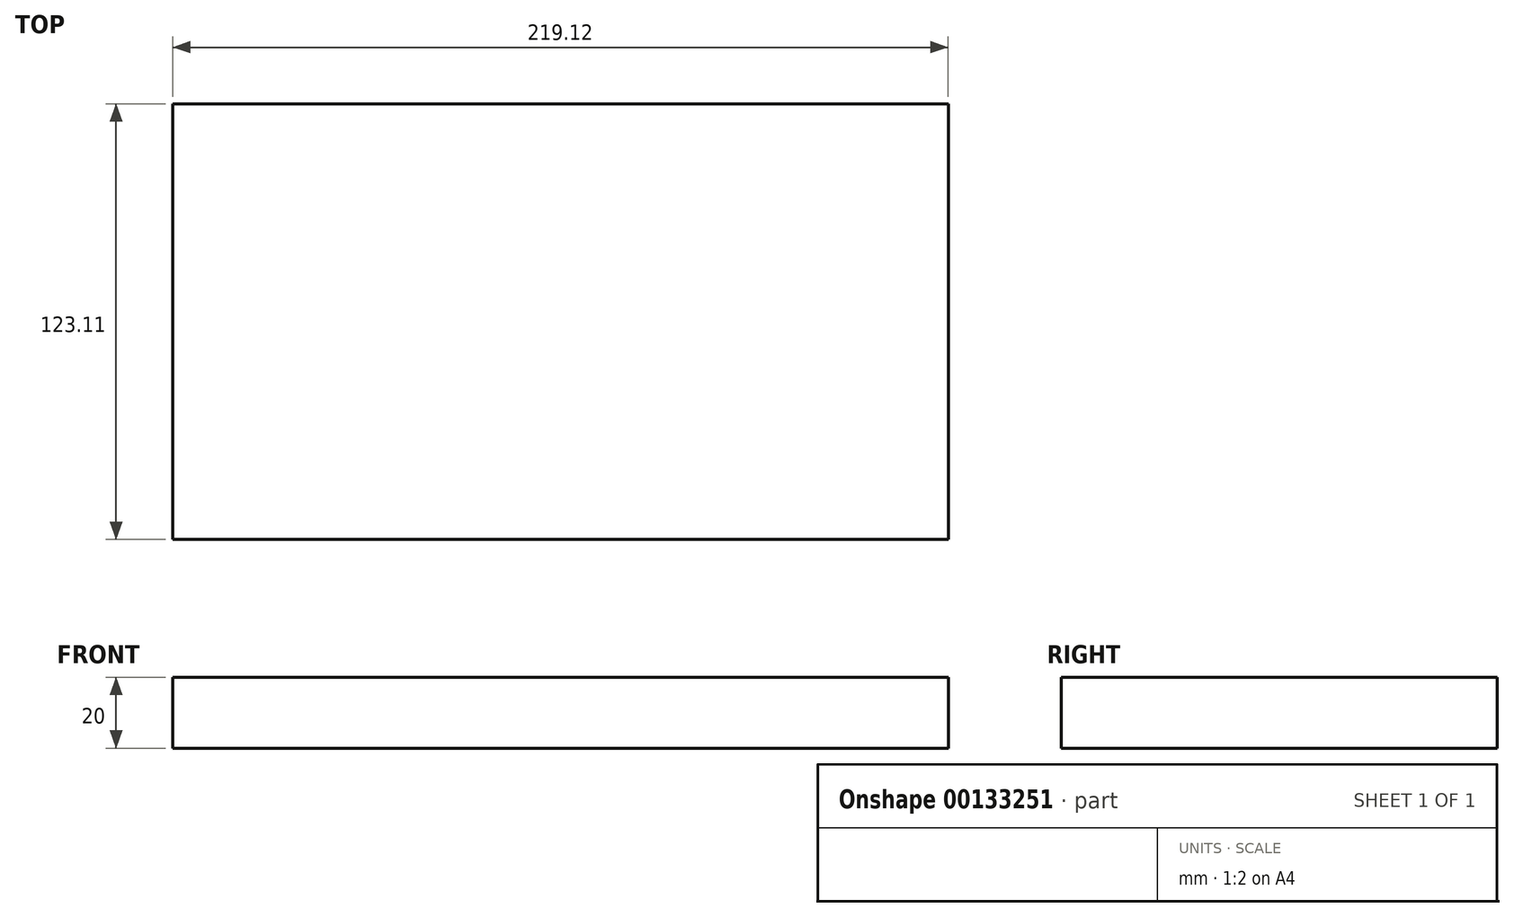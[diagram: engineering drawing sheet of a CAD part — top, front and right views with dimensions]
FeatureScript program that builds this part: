
annotation { "Feature Type Name" : "Feature", "Feature Type Description" : "" }
export const myFeature = defineFeature(function(context is Context, id is Id, definition is map)
    precondition{}
    {
        {
            var Q0;
            Q0=qCreatedBy(makeId("Top.planeOp"),FACE);
            var sketch = newSketch(context, id + "F0", { "sketchPlane" : qUnion([Q0])});
            skLineSegment(sketch, "E0.bottom", {"start": v(-100.2, 60.4) * mm, "end": v(118.93, 60.4) * mm});
            skLineSegment(sketch, "E0.top", {"start": v(-100.2, -62.71) * mm, "end": v(118.93, -62.71) * mm});
            skLineSegment(sketch, "E0.left", {"start": v(-100.2, 60.4) * mm, "end": v(-100.2, -62.71) * mm});
            skLineSegment(sketch, "E0.right", {"start": v(118.93, 60.4) * mm, "end": v(118.93, -62.71) * mm});
            skSolve(sketch);
        }
        {
            var Q0;
            Q0=makeQuery(id+"F0.imprint","IMPRINT",FACE,{"disambiguationData":[TD([[makeQuery(id+"F0.imprint","IMPRINT",EDGE,{"derivedFrom":sQuery(id+"F0.wireOp",EDGE,"E0.bottom")}),-1.0]])]});
            extrude(context, id + "F1", {"entities" : qUnion([Q0]), "depth" : 20 * mm});
        }
    });
